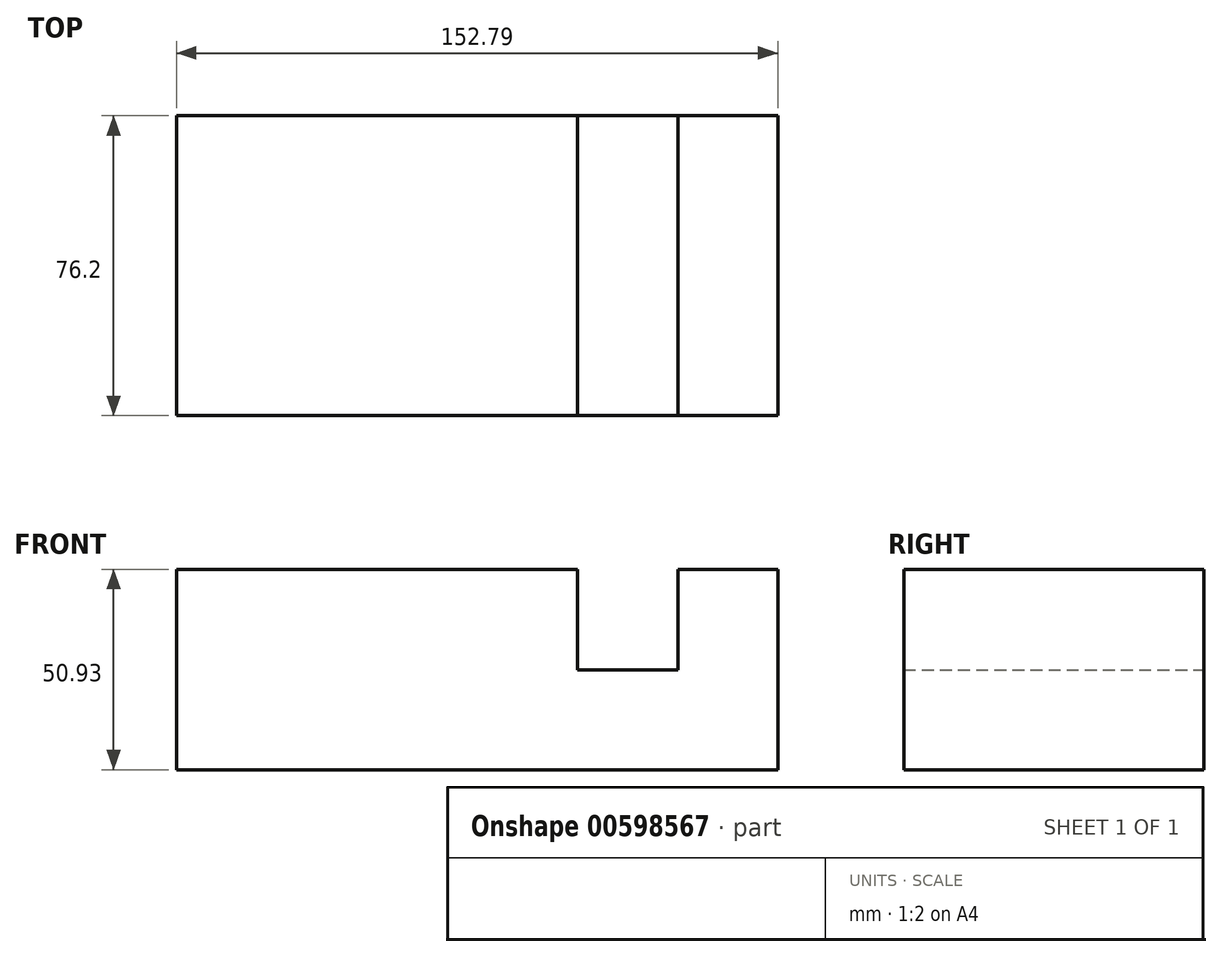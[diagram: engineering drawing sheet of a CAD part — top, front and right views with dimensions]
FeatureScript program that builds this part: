
annotation { "Feature Type Name" : "Feature", "Feature Type Description" : "" }
export const myFeature = defineFeature(function(context is Context, id is Id, definition is map)
    precondition{}
    {
        {
            var Q0;
            Q0=qCreatedBy(makeId("Front.planeOp"),FACE);
            var sketch = newSketch(context, id + "F0", { "sketchPlane" : qUnion([Q0])});
            skLineSegment(sketch, "E0", {"start": v(0, 0) * mm, "end": v(0, 50.93) * mm});
            skLineSegment(sketch, "E1", {"start": v(0, 50.93) * mm, "end": v(-25.4, 50.93) * mm});
            skLineSegment(sketch, "E2", {"start": v(-25.4, 50.93) * mm, "end": v(-25.4, 25.4) * mm});
            skLineSegment(sketch, "E3", {"start": v(-25.4, 25.4) * mm, "end": v(-50.93, 25.4) * mm});
            skLineSegment(sketch, "E4", {"start": v(-50.93, 25.4) * mm, "end": v(-50.93, 50.93) * mm});
            skLineSegment(sketch, "E5", {"start": v(-50.93, 50.93) * mm, "end": v(-152.79, 50.93) * mm});
            skLineSegment(sketch, "E6", {"start": v(-152.79, 50.93) * mm, "end": v(-152.79, 0) * mm});
            skLineSegment(sketch, "E7", {"start": v(-152.79, 0) * mm, "end": v(0, 0) * mm});
            skSolve(sketch);
        }
        {
            var Q0;
            Q0 = qSketchRegion(id + "F0", true);
            extrude(context, id + "F1", {"entities" : qUnion([Q0]), "depth" : 76.2 * mm, "offsetDistance" : 25.4 * mm});
        }
    });
